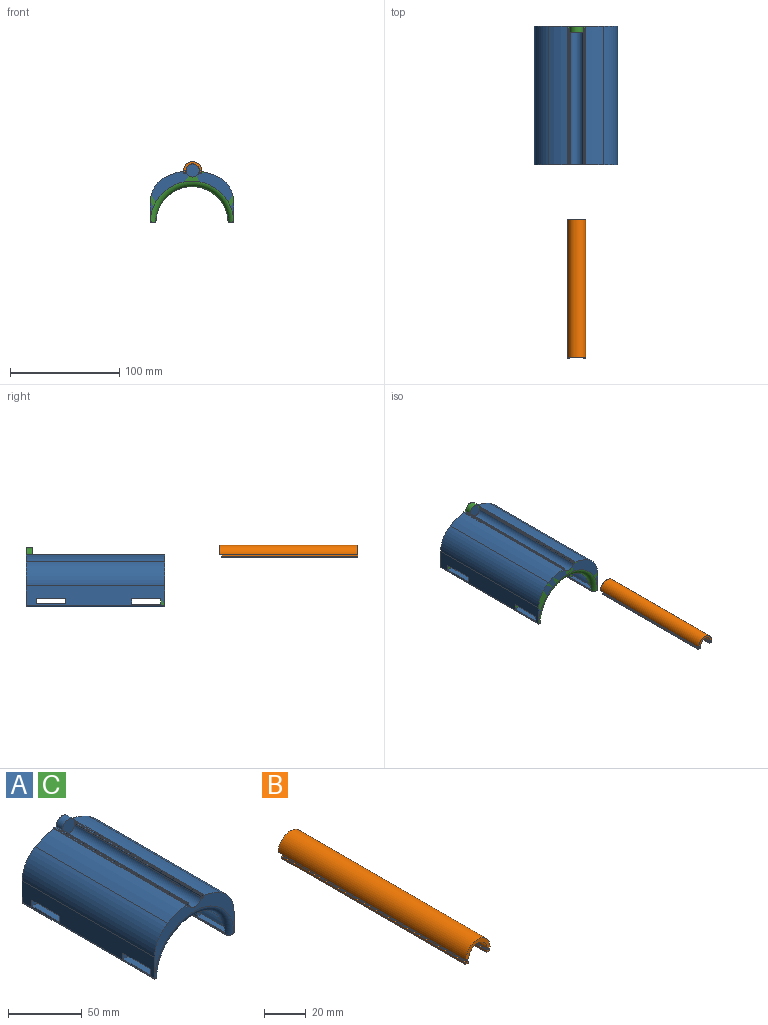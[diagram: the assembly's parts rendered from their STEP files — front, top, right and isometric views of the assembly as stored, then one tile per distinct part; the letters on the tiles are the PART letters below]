
ASSEMBLY  parts=3 mates=1
PART A: 62 faces, bbox 90.3x127x53.7 mm
  f0: cylinder r=6.04mm len=12.07mm, axis (0,-1,0), area 0.5mm2, adj f1,f2,f6,f60
  f1: plane 127x2.22mm, normal (0,0,1), area 182.6mm2, adj f0,f3,f6,f24,f25,f30,f31,f34
  f2: plane 127x2.22mm, normal (0,0,1), area 182.6mm2, adj f0,f3,f6,f24,f26,f38,f39,f42
  f3: plane 76.2x46.41mm, normal (0,-1,0), area 852mm2, adj f1,f2,f4,f5,f7,f11,f12,f13
  f4: cylinder r=50.8mm len=127mm, axis (0,-1,0), area 2257.2mm2, adj f3,f6,f12,f26
  f5: plane 127x17.61mm, normal (-1,0,0), area 1965mm2, adj f3,f6,f13,f20,f47,f48,f49,f50
  f6: plane 76.2x46.41mm, normal (0,1,0), area 860.1mm2, adj f0,f1,f2,f4,f5,f7,f11,f12
  f7: plane 127x17.61mm, normal (1,0,0), area 1965mm2, adj f3,f6,f12,f16,f43,f44,f45,f46
  f8: plane 124.46x2.57mm, normal (0,0,-1), area 319.3mm2, adj f14,f15,f16,f17,f22,f23
  f9: cylinder r=33.02mm len=116.84mm, axis (0,-1,0), area 11275.7mm2, adj f15,f19,f22,f23,f43,f44,f46,f47
  f10: plane 124.46x2.57mm, normal (0,0,-1), area 319.3mm2, adj f18,f19,f20,f21,f22,f23
  f11: cylinder r=50.8mm len=127mm, axis (0,-1,0), area 2399.8mm2, adj f3,f6,f13,f25
  f12: cylinder r=25.4mm len=127mm, axis (0,-1,0), area 3378mm2, adj f3,f4,f6,f7
  f13: cylinder r=25.4mm len=127mm, axis (0,-1,0), area 3378mm2, adj f3,f5,f6,f11
  f14: cylinder r=1.27mm len=3.36mm, axis (-1,0,0), area 2.7mm2, adj f3,f8,f16,f22
  f15: cylinder r=1.27mm len=123.5mm, axis (0,-1,0), area 233.6mm2, adj f8,f9,f22,f23
  f16: cylinder r=1.27mm len=127mm, axis (0,-1,0), area 250.8mm2, adj f7,f8,f14,f17
  f17: cylinder r=1.27mm len=3.36mm, axis (-1,0,0), area 2.7mm2, adj f6,f8,f16,f23
  f18: cylinder r=1.27mm len=3.36mm, axis (-1,0,0), area 2.7mm2, adj f3,f10,f20,f22
  f19: cylinder r=1.27mm len=123.5mm, axis (0,-1,0), area 233.6mm2, adj f9,f10,f22,f23
  f20: cylinder r=1.27mm len=127mm, axis (0,1,0), area 250.8mm2, adj f5,f10,f18,f21
  f21: cylinder r=1.27mm len=3.36mm, axis (-1,0,0), area 2.7mm2, adj f6,f10,f20,f23
  f22: torus R=38.1mm, axis (0,1,0), area 849.5mm2, adj f3,f8,f9,f10,f14,f15,f18,f19
  f23: torus R=38.1mm, axis (0,1,0), area 863.4mm2, adj f6,f8,f9,f10,f15,f17,f19,f21
  f24: cylinder r=6.04mm len=121.08mm, axis (0,-1,0), area 2296.8mm2, adj f1,f2,f3,f61
  f25: cylinder r=8.26mm len=127mm, axis (0,-1,0), area 73.7mm2, adj f1,f3,f6,f11
  f26: cylinder r=8.26mm len=127mm, axis (0,-1,0), area 97.7mm2, adj f2,f3,f4,f6
  f27: plane 124.46x2.22mm, normal (0,0,1), area 276.2mm2, adj f3,f28,f33,f34
  f28: plane 124.46x1.35mm, normal (-1,0,0), area 167.5mm2, adj f3,f27,f29,f34
  f29: plane 124.46x0.71mm, normal (0,0,-1), area 88.5mm2, adj f3,f28,f30,f34
  f30: plane 124.46x1.35mm, normal (-1,0,0), area 167.6mm2, adj f1,f3,f29,f34
  f31: plane 124.46x1.35mm, normal (1,0,0), area 167.5mm2, adj f1,f3,f32,f34
  f32: plane 124.46x0.71mm, normal (0,0,-1), area 88.5mm2, adj f3,f31,f33,f34
  f33: plane 124.46x1.35mm, normal (1,0,0), area 167.5mm2, adj f3,f27,f32,f34
  f34: plane 2.69x2.22mm, normal (0,-1,0), area 4.1mm2, adj f1,f27,f28,f29,f30,f31,f32,f33
  f35: plane 124.46x2.22mm, normal (0,0,1), area 276.2mm2, adj f3,f36,f41,f42
  f36: plane 124.46x1.35mm, normal (-1,0,0), area 167.5mm2, adj f3,f35,f37,f42
  f37: plane 124.46x0.71mm, normal (0,0,-1), area 88.5mm2, adj f3,f36,f38,f42
  f38: plane 124.46x1.35mm, normal (-1,0,0), area 168.3mm2, adj f2,f3,f37,f42
  f39: plane 124.46x1.35mm, normal (1,0,0), area 168.3mm2, adj f2,f3,f40,f42
  f40: plane 124.46x0.71mm, normal (0,0,-1), area 88.5mm2, adj f3,f39,f41,f42
  f41: plane 124.46x1.35mm, normal (1,0,0), area 167.5mm2, adj f3,f35,f40,f42
  f42: plane 2.7x2.22mm, normal (0,-1,0), area 4.1mm2, adj f2,f35,f36,f37,f38,f39,f40,f41
  f43: plane 26.69x5.92mm, normal (0,0,-1), area 157.3mm2, adj f7,f9,f22,f45,f46
  f44: plane 26.68x5.17mm, normal (0,0,1), area 137.4mm2, adj f7,f9,f22,f45,f46
  f45: plane 5.72x5.08mm, normal (0,1,0), area 26.8mm2, adj f7,f22,f43,f44
  f46: plane 5.9x5.08mm, normal (0,-1,0), area 27.7mm2, adj f7,f9,f43,f44
  f47: plane 5.9x5.08mm, normal (0,-1,0), area 27.7mm2, adj f5,f9,f49,f50
  f48: plane 5.72x5.08mm, normal (0,1,0), area 26.8mm2, adj f5,f22,f49,f50
  f49: plane 26.68x5.16mm, normal (0,0,1), area 137.4mm2, adj f5,f9,f22,f47,f48
  f50: plane 26.69x5.92mm, normal (0,0,-1), area 157.3mm2, adj f5,f9,f22,f47,f48
  f51: plane 26.67x6.01mm, normal (0,0,-1), area 160.3mm2, adj f5,f9,f52,f54
  f52: plane 6.01x5.08mm, normal (0,-1,0), area 28.1mm2, adj f5,f9,f51,f53
  f53: plane 26.67x5.19mm, normal (0,0,1), area 138.4mm2, adj f5,f9,f52,f54
  f54: plane 6.01x5.08mm, normal (0,1,0), area 28.1mm2, adj f5,f9,f51,f53
  f55: plane 6.01x5.08mm, normal (0,1,0), area 28.1mm2, adj f7,f9,f56,f58
  f56: plane 26.67x5.19mm, normal (0,0,1), area 138.4mm2, adj f7,f9,f55,f57
  f57: plane 6.01x5.08mm, normal (0,-1,0), area 28.1mm2, adj f7,f9,f56,f58
  f58: plane 26.67x6.01mm, normal (0,0,-1), area 160.3mm2, adj f7,f9,f55,f57
  f59: cylinder r=6.06mm len=12.11mm, axis (0,-1,0), area 111.1mm2, adj f1,f2,f60,f61
  f60: plane 12.11x12.01mm, normal (0,1,0), area 113.9mm2, adj f0,f1,f2,f59
  f61: plane 12.11x12.01mm, normal (0,-1,0), area 113.9mm2, adj f1,f2,f24,f59
PART B: 22 faces, bbox 16.5x127x10.9 mm
  f0: plane 127x2.22mm, normal (0,0,-1), area 195.3mm2, adj f2,f3,f4,f5,f14,f20,f21
  f1: plane 127x2.22mm, normal (0,0,-1), area 195.3mm2, adj f2,f3,f4,f5,f6,f7,f13
  f2: cylinder r=6.03mm len=127mm, axis (0,1,0), area 2406.9mm2, adj f0,f1,f4,f5
  f3: cylinder r=8.26mm len=127mm, axis (0,1,0), area 3293.6mm2, adj f0,f1,f4,f5
  f4: plane 16.51x10.87mm, normal (0,-1,0), area 56.6mm2, adj f0,f1,f2,f3,f6,f7,f8,f9
  f5: plane 16.51x8.26mm, normal (0,1,0), area 49.9mm2, adj f0,f1,f2,f3
  f6: plane 124.46x1.42mm, normal (1,0,0), area 177mm2, adj f1,f4,f12,f13
  f7: plane 124.46x1.42mm, normal (-1,0,0), area 177mm2, adj f1,f4,f8,f13
  f8: plane 124.46x0.64mm, normal (0,0,1), area 79mm2, adj f4,f7,f9,f13
  f9: plane 124.46x1.19mm, normal (-1,0,0), area 148.6mm2, adj f4,f8,f10,f13
  f10: plane 124.46x1.97mm, normal (0,0,-1), area 245mm2, adj f4,f9,f11,f13
  f11: plane 124.46x1.19mm, normal (1,0,0), area 148.6mm2, adj f4,f10,f12,f13
  f12: plane 124.46x0.64mm, normal (0,0,1), area 79mm2, adj f4,f6,f11,f13
  f13: plane 2.62x1.97mm, normal (0,1,0), area 3.3mm2, adj f1,f6,f7,f8,f9,f10,f11,f12
  f14: plane 124.46x1.42mm, normal (-1,0,0), area 177mm2, adj f0,f4,f15,f21
  f15: plane 124.46x0.64mm, normal (0,0,1), area 79mm2, adj f4,f14,f16,f21
  f16: plane 124.46x1.19mm, normal (-1,0,0), area 148.6mm2, adj f4,f15,f17,f21
  f17: plane 124.46x1.97mm, normal (0,0,-1), area 245mm2, adj f4,f16,f18,f21
  f18: plane 124.46x1.19mm, normal (1,0,0), area 148.6mm2, adj f4,f17,f19,f21
  f19: plane 124.46x0.64mm, normal (0,0,1), area 79mm2, adj f4,f18,f20,f21
  f20: plane 124.46x1.42mm, normal (1,0,0), area 177mm2, adj f0,f4,f19,f21
  f21: plane 2.62x1.97mm, normal (0,1,0), area 3.3mm2, adj f0,f14,f15,f16,f17,f18,f19,f20
PART C: same geometry as A
PLACE A t=(-43.27,45.9,19.74)mm fixed
PLACE B t=(-43.27,-157.79,54.72)mm
PLACE C t=(-43.27,45.9,19.74)mm fixed
MATE slider C.f0 <-> B.f2  axis (0,-1,0) through (-43.27,-44.7,54.72)mm
